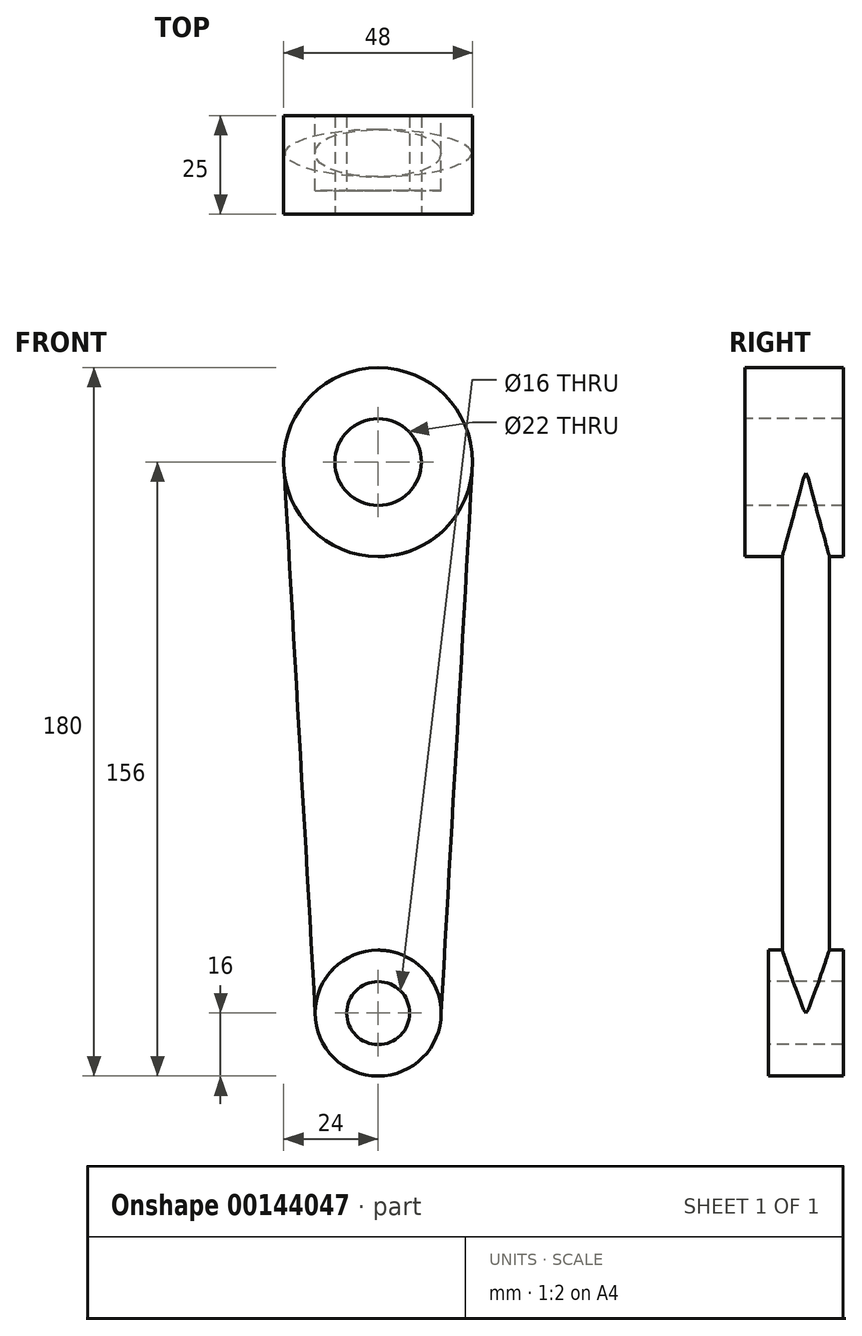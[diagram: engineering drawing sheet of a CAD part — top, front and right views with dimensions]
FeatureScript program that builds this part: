
annotation { "Feature Type Name" : "Feature", "Feature Type Description" : "" }
export const myFeature = defineFeature(function(context is Context, id is Id, definition is map)
    precondition{}
    {
        {
            var Q0;
            Q0=qCreatedBy(makeId("Front.planeOp"),FACE);
            var sketch = newSketch(context, id + "F0", { "sketchPlane" : qUnion([Q0])});
            skCircle(sketch, "E0", {"center": v(0, 0) * mm, "radius": 8 * mm});
            skCircle(sketch, "E1", {"center": v(0, 0) * mm, "radius": 16 * mm});
            skCircle(sketch, "E2", {"center": v(0, 140) * mm, "radius": 11 * mm});
            skCircle(sketch, "E3", {"center": v(0, 140) * mm, "radius": 24 * mm});
            skLineSegment(sketch, "E4", {"start": v(0, 140) * mm, "end": v(0, 0) * mm, "construction": true});
            skSolve(sketch);
        }
        {
            var Q0;
            Q0=makeQuery(id+"F0.imprint","IMPRINT",FACE,{"disambiguationData":[TD([[makeQuery(id+"F0.imprint","IMPRINT",EDGE,{"derivedFrom":sQuery(id+"F0.wireOp",EDGE,"E2")}),-1.0]])]});
            var Q1;
            Q1=makeQuery(id+"F0.imprint","IMPRINT",FACE,{"disambiguationData":[TD([[makeQuery(id+"F0.imprint","IMPRINT",EDGE,{"derivedFrom":sQuery(id+"F0.wireOp",EDGE,"E2")}),1.0]])]});
            extrude(context, id + "F1", {"entities" : qUnion([Q0, Q1]), "depth" : 25 * mm});
        }
        {
            var Q0;
            Q0=makeQuery(id+"F0.imprint","IMPRINT",FACE,{"disambiguationData":[TD([[makeQuery(id+"F0.imprint","IMPRINT",EDGE,{"derivedFrom":sQuery(id+"F0.wireOp",EDGE,"E0")}),-1.0]])]});
            var Q1;
            Q1=makeQuery(id+"F0.imprint","IMPRINT",FACE,{"disambiguationData":[TD([[makeQuery(id+"F0.imprint","IMPRINT",EDGE,{"derivedFrom":sQuery(id+"F0.wireOp",EDGE,"E0")}),1.0]])]});
            extrude(context, id + "F2", {"entities" : qUnion([Q0, Q1]), "depth" : 19 * mm});
        }
        {
            var Q0;
            Q0=qCreatedBy(makeId("Top.planeOp"),FACE);
            var sketch = newSketch(context, id + "F3", { "sketchPlane" : qUnion([Q0])});
            skLineSegment(sketch, "E5.0", {"start": v(16, -19) * mm, "end": v(-16, -19) * mm});
            skLineSegment(sketch, "E5.1", {"start": v(16, 0) * mm, "end": v(-16, 0) * mm});
            skLineSegment(sketch, "E6", {"start": v(16, -19) * mm, "end": v(16, 0) * mm, "construction": true});
            skPoint(sketch, "E7", {"position": v(16, -9.5) * mm});
            skEllipse(sketch, "E8", {"center": v(0, -9.5) * mm, "majorRadius": 16 * mm, "minorRadius": 6 * mm, "majorAxis": v(1, 0)});
            skSolve(sketch);
        }
        {
            var Q0;
            Q0=qCreatedBy(makeId("Top.planeOp"),FACE);
            cPlane(context, id + "F4", {"entities" : qUnion([Q0]), "cplaneType" : CPlaneType.OFFSET, "offset" : 140 * mm, "width" : 150 * mm, "height" : 150 * mm});
        }
        {
            var Q0;
            Q0=qCreatedBy(id+"F4.planeOp",FACE);
            var sketch = newSketch(context, id + "F5", { "sketchPlane" : qUnion([Q0])});
            skEllipse(sketch, "E9", {"center": v(0, -9.5) * mm, "majorRadius": 24 * mm, "minorRadius": 6 * mm, "majorAxis": v(1, 0)});
            skLineSegment(sketch, "E10.0", {"start": v(24, 0) * mm, "end": v(-24, 0) * mm});
            skLineSegment(sketch, "E10.1", {"start": v(24, -25) * mm, "end": v(-24, -25) * mm});
            skLineSegment(sketch, "E11", {"start": v(24, 0) * mm, "end": v(24, -25) * mm, "construction": true});
            skPoint(sketch, "E12", {"position": v(24, -9.5) * mm});
            skSolve(sketch);
        }
        {
            var Q0;
            Q0=makeQuery(id+"F5.imprint","IMPRINT",FACE,{"disambiguationData":[TD([[makeQuery(id+"F5.imprint","IMPRINT",EDGE,{"derivedFrom":sQuery(id+"F5.wireOp",EDGE,"E9")}),1.0]])]});
            var Q1;
            Q1=makeQuery(id+"F3.imprint","IMPRINT",FACE,{"disambiguationData":[TD([[makeQuery(id+"F3.imprint","IMPRINT",EDGE,{"derivedFrom":sQuery(id+"F3.wireOp",EDGE,"E8")}),1.0]])]});
            loft(context, id + "F6", {"operationType" : NewBodyOperationType.ADD, "sheetProfilesArray" : [{ "sheetProfileEntities" : qUnion([Q0]) }, { "sheetProfileEntities" : qUnion([Q1]) }]});
        }
        {
            var Q0;
            Q0=qCreatedBy(makeId("Front.planeOp"),FACE);
            var sketch = newSketch(context, id + "F7", { "sketchPlane" : qUnion([Q0])});
            skCircle(sketch, "E13.0", {"center": v(0, 0) * mm, "radius": 8 * mm});
            skCircle(sketch, "E13.1", {"center": v(0, 140) * mm, "radius": 11 * mm});
            skSolve(sketch);
        }
        {
            var Q0;
            Q0 = qSketchRegion(id + "F7", true);
            extrude(context, id + "F8", {"entities" : qUnion([Q0]), "operationType" : NewBodyOperationType.REMOVE, "endBound" : BoundingType.THROUGH_ALL, "oppositeDirection" : true, "depth" : 25 * mm, "hasSecondDirection" : true, "secondDirectionBound" : SecondDirectionBoundingType.THROUGH_ALL, "secondDirectionOppositeDirection" : false, "secondDirectionDepth" : 25 * mm});
        }
    });
